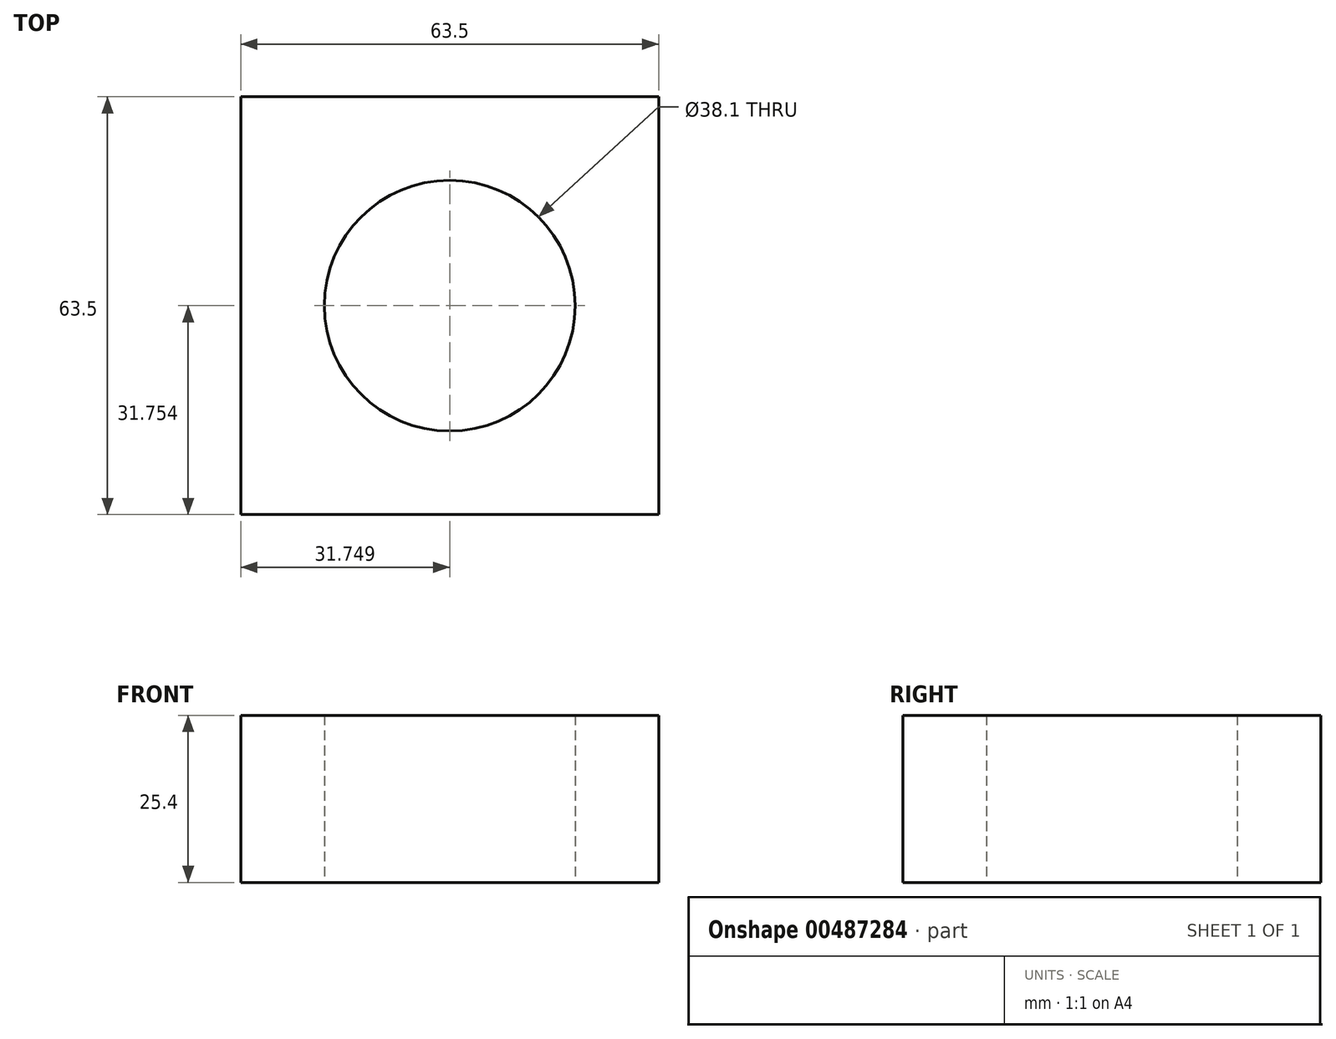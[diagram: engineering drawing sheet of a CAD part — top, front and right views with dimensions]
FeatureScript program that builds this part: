
annotation { "Feature Type Name" : "Feature", "Feature Type Description" : "" }
export const myFeature = defineFeature(function(context is Context, id is Id, definition is map)
    precondition{}
    {
        {
            var Q0;
            Q0=qCreatedBy(makeId("Top.planeOp"),FACE);
            var sketch = newSketch(context, id + "F0", { "sketchPlane" : qUnion([Q0])});
            skLineSegment(sketch, "E0", {"start": v(-24.7, -29.66) * mm, "end": v(38.8, -29.66) * mm});
            skLineSegment(sketch, "E1", {"start": v(38.8, -29.66) * mm, "end": v(38.8, 33.84) * mm});
            skLineSegment(sketch, "E2", {"start": v(38.8, 33.84) * mm, "end": v(-24.7, 33.84) * mm});
            skLineSegment(sketch, "E3", {"start": v(-24.7, 33.84) * mm, "end": v(-24.7, -29.66) * mm});
            skLineSegment(sketch, "E4", {"start": v(7.05, 33.84) * mm, "end": v(7.05, -29.66) * mm});
            skLineSegment(sketch, "E5", {"start": v(-24.7, 2.1) * mm, "end": v(38.8, 2.1) * mm});
            skCircle(sketch, "E6", {"center": v(7.05, 2.1) * mm, "radius": 19.05 * mm});
            skSolve(sketch);
        }
        {
            var Q0;
            Q0 = qSketchRegion(id + "F0", true);
            extrude(context, id + "F1", {"entities" : qUnion([Q0]), "depth" : 25.4 * mm});
        }
    });
